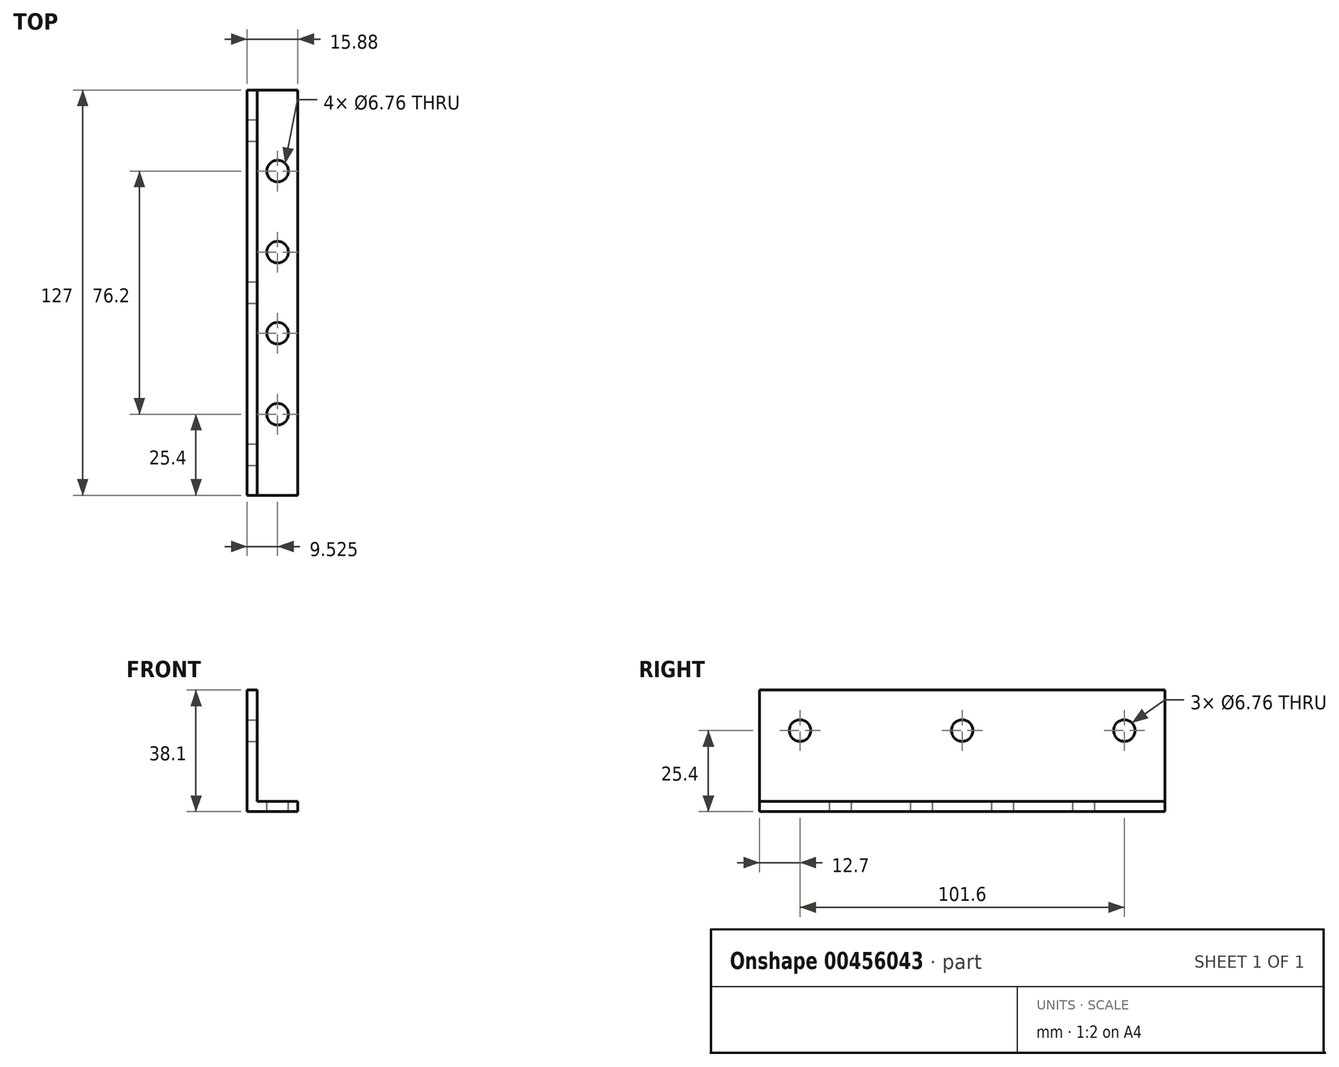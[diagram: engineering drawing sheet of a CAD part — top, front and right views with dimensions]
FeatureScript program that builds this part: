
annotation { "Feature Type Name" : "Feature", "Feature Type Description" : "" }
export const myFeature = defineFeature(function(context is Context, id is Id, definition is map)
    precondition{}
    {
        {
            var Q0;
            Q0=qCreatedBy(makeId("Front.planeOp"),FACE);
            var sketch = newSketch(context, id + "F0", { "sketchPlane" : qUnion([Q0])});
            skLineSegment(sketch, "E0", {"start": v(0, 0) * mm, "end": v(0, 38.1) * mm});
            skLineSegment(sketch, "E1", {"start": v(0, 38.1) * mm, "end": v(3.17, 38.1) * mm});
            skLineSegment(sketch, "E2", {"start": v(3.18, 38.1) * mm, "end": v(3.18, 3.17) * mm});
            skLineSegment(sketch, "E3", {"start": v(3.18, 3.17) * mm, "end": v(15.88, 3.17) * mm});
            skLineSegment(sketch, "E4", {"start": v(15.88, 3.17) * mm, "end": v(15.88, 0) * mm});
            skLineSegment(sketch, "E5", {"start": v(15.88, 0) * mm, "end": v(0, 0) * mm});
            skSolve(sketch);
        }
        {
            var Q0;
            Q0=makeQuery(id+"F0.imprint","IMPRINT",FACE,{"disambiguationData":[TD([[makeQuery(id+"F0.imprint","IMPRINT",EDGE,{"derivedFrom":sQuery(id+"F0.wireOp",EDGE,"E0")}),-1.0]])]});
            extrude(context, id + "F1", {"entities" : qUnion([Q0]), "depth" : 127 * mm});
        }
        {
            var Q0;
            Q0=makeQuery(id+"F1.opExtrude","SWEPT_FACE",FACE,{"disambiguationData":[OSD([sQuery(id+"F0.wireOp",EDGE,"E2")])]});
            var sketch = newSketch(context, id + "F2", { "sketchPlane" : qUnion([Q0])});
            skPoint(sketch, "E6", {"position": v(-114.3, 25.4) * mm});
            skPoint(sketch, "E7.1.0.0", {"position": v(-63.5, 25.4) * mm});
            skPoint(sketch, "E7.2.0.0", {"position": v(-12.7, 25.4) * mm});
            skLineSegment(sketch, "E7.direction1", {"start": v(-114.3, 25.4) * mm, "end": v(-63.5, 25.4) * mm, "construction": true});
            skSolve(sketch);
        }
        {
            var Q0;
            Q0=sQuery(id+"F2.wireOp",VERTEX,"E6");
            var Q1;
            Q1=sQuery(id+"F2.wireOp",VERTEX,"E7.1.0.0");
            var Q2;
            Q2=sQuery(id+"F2.wireOp",VERTEX,"E7.2.0.0");
            var Q3;
            Q3=makeQuery(id+"F1.opExtrude","SWEPT_BODY",BODY,{"disambiguationData":[OSD([sQuery(id+"F0.wireOp",EDGE,"E0"),sQuery(id+"F0.wireOp",EDGE,"E1"),sQuery(id+"F0.wireOp",EDGE,"E2"),sQuery(id+"F0.wireOp",EDGE,"E3"),sQuery(id+"F0.wireOp",EDGE,"E4"),sQuery(id+"F0.wireOp",EDGE,"E5")])]});
            hole(context, id + "F3", {"style" : HoleStyle.SIMPLE, "endStyle" : HoleEndStyle.THROUGH, "standardTappedOrClearance" : lookupTablePath({ "standard" : "ANSI", "fit" : "Normal (ASME)", "size" : "1/4", "type" : "Clearance" }), "standardBlindInLast" : lookupTablePath({ "fit" : "Free", "standard" : "ANSI", "size" : "1/4", "type" : "Clearance" }), "holeDiameter" : 6.76 * mm, "isTappedThrough" : true, "tappedDepth" : 8.9 * mm, "tapClearance" : 3, "locations" : qUnion([Q0, Q1, Q2]), "scope" : qUnion([Q3])});
        }
        {
            var Q0;
            Q0=makeQuery(id+"F1.opExtrude","SWEPT_FACE",FACE,{"disambiguationData":[OSD([sQuery(id+"F0.wireOp",EDGE,"E3")])]});
            var sketch = newSketch(context, id + "F4", { "sketchPlane" : qUnion([Q0])});
            skPoint(sketch, "E8", {"position": v(9.52, -101.6) * mm});
            skPoint(sketch, "E9.0.1.0", {"position": v(9.52, -76.2) * mm});
            skPoint(sketch, "E9.0.2.0", {"position": v(9.52, -50.8) * mm});
            skPoint(sketch, "E9.0.3.0", {"position": v(9.52, -25.4) * mm});
            skPoint(sketch, "E9.0.4.0", {"position": v(9.52, 0) * mm});
            skLineSegment(sketch, "E9.direction1", {"start": v(9.52, -101.6) * mm, "end": v(38.1, -101.6) * mm, "construction": true});
            skLineSegment(sketch, "E9.direction2", {"start": v(9.52, -101.6) * mm, "end": v(9.52, -76.2) * mm, "construction": true});
            skSolve(sketch);
        }
        {
            var Q0;
            Q0=sQuery(id+"F4.wireOp",VERTEX,"E8");
            var Q1;
            Q1=sQuery(id+"F4.wireOp",VERTEX,"E9.0.3.0");
            var Q2;
            Q2=sQuery(id+"F4.wireOp",VERTEX,"E9.0.1.0");
            var Q3;
            Q3=sQuery(id+"F4.wireOp",VERTEX,"E9.0.2.0");
            var Q4;
            Q4=makeQuery(id+"F1.opExtrude","SWEPT_BODY",BODY,{"disambiguationData":[OSD([sQuery(id+"F0.wireOp",EDGE,"E0"),sQuery(id+"F0.wireOp",EDGE,"E1"),sQuery(id+"F0.wireOp",EDGE,"E2"),sQuery(id+"F0.wireOp",EDGE,"E3"),sQuery(id+"F0.wireOp",EDGE,"E4"),sQuery(id+"F0.wireOp",EDGE,"E5")])]});
            hole(context, id + "F5", {"style" : HoleStyle.SIMPLE, "endStyle" : HoleEndStyle.THROUGH, "standardTappedOrClearance" : lookupTablePath({ "standard" : "ANSI", "fit" : "Normal (ASME)", "size" : "1/4", "type" : "Clearance" }), "standardBlindInLast" : lookupTablePath({ "fit" : "Free", "standard" : "ANSI", "size" : "1/4", "type" : "Clearance" }), "holeDiameter" : 6.76 * mm, "isTappedThrough" : true, "tappedDepth" : 8.9 * mm, "tapClearance" : 3, "locations" : qUnion([Q0, Q1, Q2, Q3]), "scope" : qUnion([Q4])});
        }
    });
